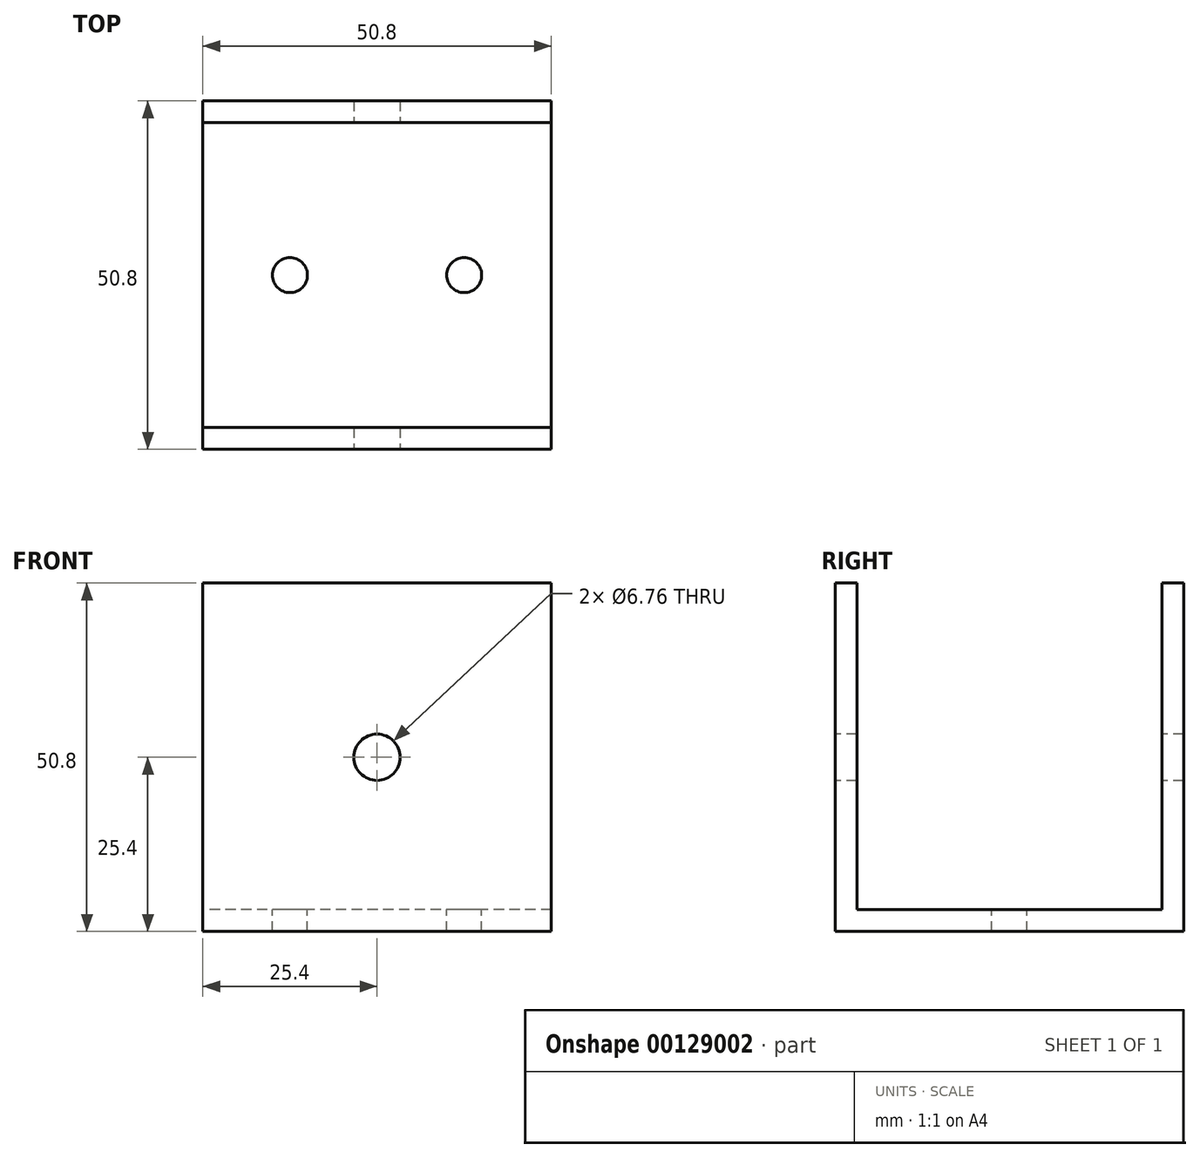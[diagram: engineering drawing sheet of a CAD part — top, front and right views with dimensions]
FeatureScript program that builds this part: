
annotation { "Feature Type Name" : "Feature", "Feature Type Description" : "" }
export const myFeature = defineFeature(function(context is Context, id is Id, definition is map)
    precondition{}
    {
        {
            var Q0;
            Q0=qCreatedBy(makeId("Right.planeOp"),FACE);
            var sketch = newSketch(context, id + "F0", { "sketchPlane" : qUnion([Q0])});
            skLineSegment(sketch, "E0", {"start": v(-25.4, 0) * mm, "end": v(25.4, 0) * mm});
            skLineSegment(sketch, "E1", {"start": v(25.4, 0) * mm, "end": v(25.4, 50.8) * mm});
            skLineSegment(sketch, "E2", {"start": v(25.4, 50.8) * mm, "end": v(22.22, 50.8) * mm});
            skLineSegment(sketch, "E3", {"start": v(22.22, 50.8) * mm, "end": v(22.22, 3.18) * mm});
            skLineSegment(sketch, "E4", {"start": v(22.22, 3.18) * mm, "end": v(-22.22, 3.17) * mm});
            skLineSegment(sketch, "E5", {"start": v(-22.22, 3.18) * mm, "end": v(-22.22, 50.8) * mm});
            skLineSegment(sketch, "E6", {"start": v(-22.22, 50.8) * mm, "end": v(-25.4, 50.8) * mm});
            skLineSegment(sketch, "E7", {"start": v(-25.4, 50.8) * mm, "end": v(-25.4, 0) * mm});
            skLineSegment(sketch, "E8", {"start": v(0, 0) * mm, "end": v(0, 3.17) * mm});
            skSolve(sketch);
        }
        {
            var Q0;
            {var subQ0=sQuery(id+"F0.wireOp",EDGE,"E5");Q0=makeQuery(id+"F0.imprint","IMPRINT",FACE,{"disambiguationData":[TD([[makeQuery(id+"F0.imprint","IMPRINT",EDGE,{"derivedFrom":subQ0}),1.0]])]});}
            var Q1;
            {var subQ2=sQuery(id+"F0.wireOp",EDGE,"E1");Q1=makeQuery(id+"F0.imprint","IMPRINT",FACE,{"disambiguationData":[TD([[makeQuery(id+"F0.imprint","IMPRINT",EDGE,{"derivedFrom":subQ2}),1.0]])]});}
            extrude(context, id + "F1", {"entities" : qUnion([Q0, Q1]), "endBound" : BoundingType.SYMMETRIC, "depth" : 50.8 * mm});
        }
        {
            var Q0;
            Q0=makeQuery(id+"F1.opExtrude","SWEPT_FACE",FACE,{"disambiguationData":[OSD([sQuery(id+"F0.wireOp",EDGE,"E4")])]});
            var sketch = newSketch(context, id + "F2", { "sketchPlane" : qUnion([Q0])});
            skLineSegment(sketch, "E9", {"start": v(0, -13.46) * mm, "end": v(0, 12.28) * mm});
            skLineSegment(sketch, "E10", {"start": v(0, 12.28) * mm, "end": v(0, 0) * mm});
            skLineSegment(sketch, "E11", {"start": v(0, 0) * mm, "end": v(13.72, 0) * mm});
            skPoint(sketch, "E12", {"position": v(-12.7, 0) * mm});
            skPoint(sketch, "E13", {"position": v(12.7, 0) * mm});
            skSolve(sketch);
        }
        {
            var Q0;
            Q0=sQuery(id+"F2.wireOp",VERTEX,"E12");
            var Q1;
            Q1=sQuery(id+"F2.wireOp",VERTEX,"E13");
            var Q2;
            Q2=makeQuery(id+"F1.opExtrude","SWEPT_BODY",BODY,{"disambiguationData":[OSD([sQuery(id+"F0.wireOp",EDGE,"E0"),sQuery(id+"F0.wireOp",EDGE,"E1"),sQuery(id+"F0.wireOp",EDGE,"E2"),sQuery(id+"F0.wireOp",EDGE,"E3"),sQuery(id+"F0.wireOp",EDGE,"E4"),sQuery(id+"F0.wireOp",EDGE,"E5"),sQuery(id+"F0.wireOp",EDGE,"E6"),sQuery(id+"F0.wireOp",EDGE,"E7")])]});
            hole(context, id + "F3", {"style" : HoleStyle.SIMPLE, "endStyle" : HoleEndStyle.THROUGH, "standardTappedOrClearance" : lookupTablePath({ "standard" : "ANSI", "engagement" : "75%", "pitch" : "20 tpi", "size" : "1/4", "type" : "Tapped" }), "standardBlindInLast" : lookupTablePath({ "standard" : "ANSI", "engagement" : "75%", "pitch" : "20 tpi", "size" : "1/4", "type" : "Tapped" }), "holeDiameter" : 5.1 * mm, "locations" : qUnion([Q0, Q1]), "scope" : qUnion([Q2]), "isTappedThrough" : true, "majorDiameter" : 6.35 * mm, "showTappedDepth" : true});
        }
        {
            var Q0;
            Q0=makeQuery(id+"F1.opExtrude","SWEPT_FACE",FACE,{"disambiguationData":[OSD([sQuery(id+"F0.wireOp",EDGE,"E7")])]});
            var sketch = newSketch(context, id + "F4", { "sketchPlane" : qUnion([Q0])});
            skPoint(sketch, "E14", {"position": v(0, 25.4) * mm});
            skSolve(sketch);
        }
        {
            var Q0;
            Q0=sQuery(id+"F4.wireOp",VERTEX,"E14");
            var Q1;
            Q1=makeQuery(id+"F1.opExtrude","SWEPT_BODY",BODY,{"disambiguationData":[OSD([sQuery(id+"F0.wireOp",EDGE,"E0"),sQuery(id+"F0.wireOp",EDGE,"E1"),sQuery(id+"F0.wireOp",EDGE,"E2"),sQuery(id+"F0.wireOp",EDGE,"E3"),sQuery(id+"F0.wireOp",EDGE,"E4"),sQuery(id+"F0.wireOp",EDGE,"E5"),sQuery(id+"F0.wireOp",EDGE,"E6"),sQuery(id+"F0.wireOp",EDGE,"E7")])]});
            hole(context, id + "F5", {"style" : HoleStyle.SIMPLE, "endStyle" : HoleEndStyle.THROUGH, "standardTappedOrClearance" : lookupTablePath({ "standard" : "ANSI", "fit" : "Normal (ASME)", "size" : "1/4", "type" : "Clearance" }), "standardBlindInLast" : lookupTablePath({ "fit" : "Free", "standard" : "ANSI", "size" : "1/4", "type" : "Clearance" }), "holeDiameter" : 6.76 * mm, "locations" : qUnion([Q0]), "scope" : qUnion([Q1]), "isTappedThrough" : true});
        }
    });
